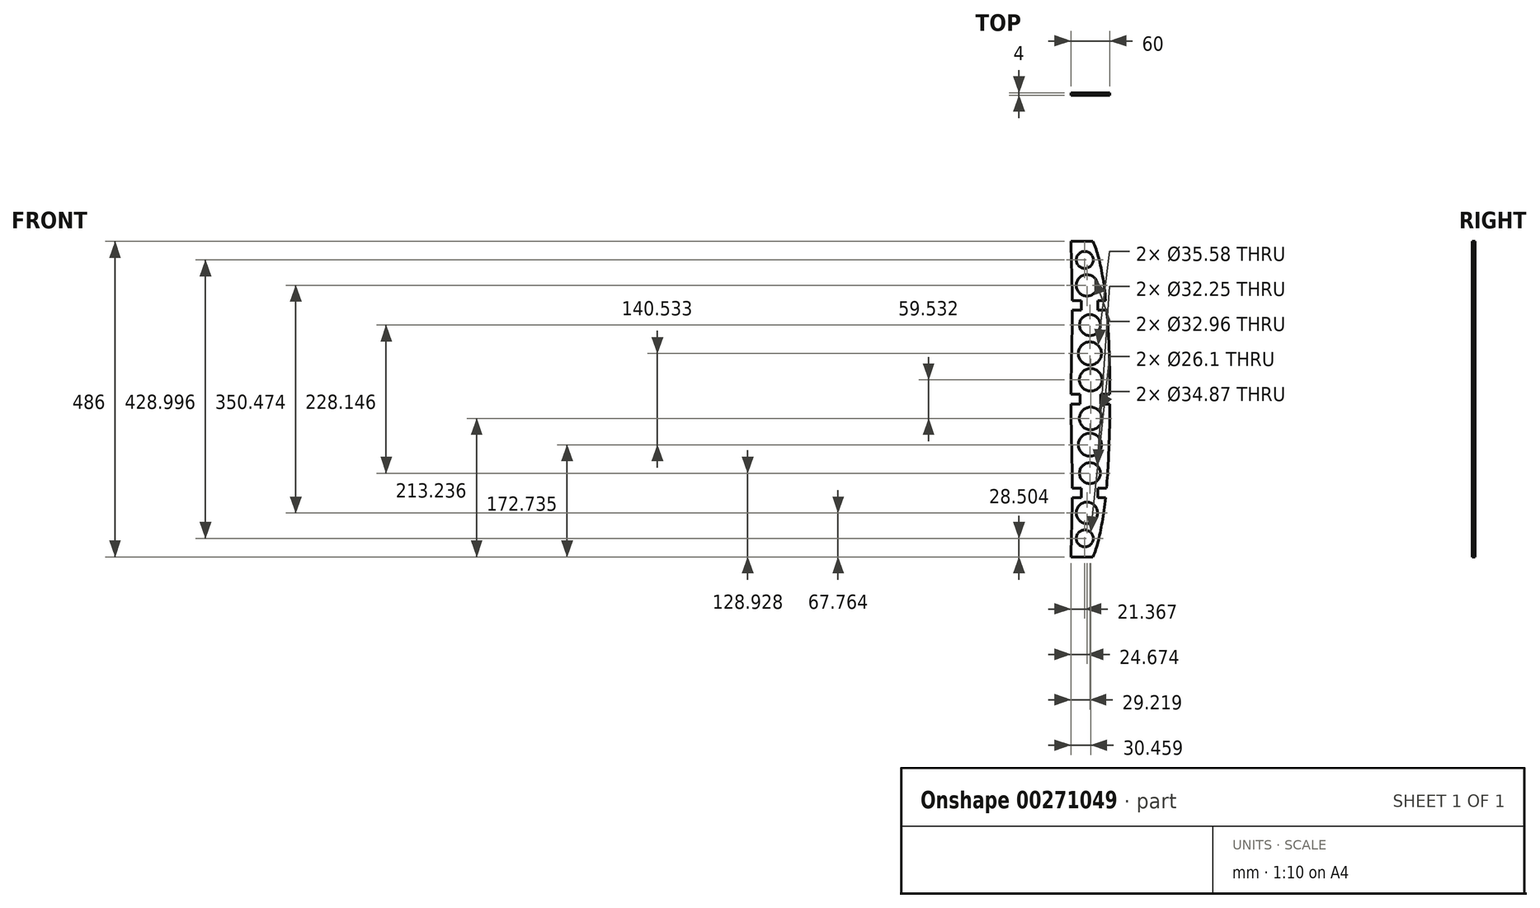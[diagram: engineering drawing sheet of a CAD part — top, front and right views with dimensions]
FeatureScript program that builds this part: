
annotation { "Feature Type Name" : "Feature", "Feature Type Description" : "" }
export const myFeature = defineFeature(function(context is Context, id is Id, definition is map)
    precondition{}
    {
        {
            var Q0;
            Q0=qCreatedBy(makeId("Front.planeOp"),FACE);
            var sketch = newSketch(context, id + "F0", { "sketchPlane" : qUnion([Q0])});
            skLineSegment(sketch, "E0", {"start": v(174.1, -34.57) * mm, "end": v(114.1, -34.57) * mm});
            skLineSegment(sketch, "E1", {"start": v(114.1, -34.57) * mm, "end": v(114.1, 208.43) * mm});
            skLineSegment(sketch, "E2", {"start": v(114.1, 208.43) * mm, "end": v(148.1, 208.43) * mm});
            skLineSegment(sketch, "E3.MirrorCS", {"start": v(114.1, -277.57) * mm, "end": v(148.1, -277.57) * mm});
            skLineSegment(sketch, "E4.MirrorCS", {"start": v(114.1, -34.57) * mm, "end": v(114.1, -277.57) * mm});
            skFitSpline(sketch, "E5", {"points": [v(148.1, 208.43) * mm, v(174.1, -34.57) * mm, v(148.1, -277.57) * mm], "startDerivative": vector(121.96, -265.32) * mm, "endDerivative": vector(-117.79, -277.83) * mm});
            skLineSegment(sketch, "E6", {"start": v(114.1, 86.93) * mm, "end": v(116.1, 86.93) * mm});
            skPoint(sketch, "E6.endSnap0", {"position": v(114.1, 86.93) * mm});
            skLineSegment(sketch, "E7", {"start": v(114.1, -156.07) * mm, "end": v(116.1, -156.07) * mm});
            skFitSpline(sketch, "E8", {"points": [v(114.1, 208.43) * mm, v(116.1, 86.93) * mm, v(114.1, -34.57) * mm, v(116.1, -156.07) * mm, v(114.1, -277.57) * mm], "startDerivative": vector(13.71, -486) * mm, "endDerivative": vector(-13.71, -486) * mm});
            skLineSegment(sketch, "E9", {"start": v(160.1, -34.57) * mm, "end": v(160.1, -27.07) * mm});
            skLineSegment(sketch, "E10", {"start": v(160.1, -27.07) * mm, "end": v(174.1, -27.07) * mm});
            skLineSegment(sketch, "E11", {"start": v(128.1, -34.57) * mm, "end": v(128.1, -27.07) * mm});
            skLineSegment(sketch, "E12", {"start": v(128.1, -27.07) * mm, "end": v(114.1, -27.07) * mm});
            skLineSegment(sketch, "E13.MirrorCS", {"start": v(160.1, -34.57) * mm, "end": v(160.1, -42.07) * mm});
            skLineSegment(sketch, "E14.MirrorCS", {"start": v(160.1, -42.07) * mm, "end": v(174.1, -42.07) * mm});
            skLineSegment(sketch, "E15.MirrorCS", {"start": v(128.1, -34.57) * mm, "end": v(128.1, -42.07) * mm});
            skLineSegment(sketch, "E16.MirrorCS", {"start": v(128.1, -42.07) * mm, "end": v(114.1, -42.07) * mm});
            skLineSegment(sketch, "E17", {"start": v(196.65, 109.93) * mm, "end": v(78.2, 109.93) * mm});
            skLineSegment(sketch, "E18", {"start": v(155.24, 109.93) * mm, "end": v(155.24, 102.43) * mm});
            skLineSegment(sketch, "E19", {"start": v(155.24, 102.43) * mm, "end": v(169.24, 102.43) * mm});
            skLineSegment(sketch, "E20", {"start": v(130.15, 109.93) * mm, "end": v(130.15, 102.43) * mm});
            skLineSegment(sketch, "E21", {"start": v(130.15, 102.43) * mm, "end": v(116.15, 102.43) * mm});
            skLineSegment(sketch, "E22.MirrorCS", {"start": v(130.15, 109.93) * mm, "end": v(130.15, 117.43) * mm});
            skLineSegment(sketch, "E23.MirrorCS", {"start": v(130.15, 117.43) * mm, "end": v(116.15, 117.43) * mm});
            skLineSegment(sketch, "E24.MirrorCS", {"start": v(155.24, 109.93) * mm, "end": v(155.24, 117.43) * mm});
            skLineSegment(sketch, "E25.MirrorCS", {"start": v(155.24, 117.43) * mm, "end": v(169.24, 117.43) * mm});
            skLineSegment(sketch, "E26", {"start": v(116.15, 117.43) * mm, "end": v(115.35, 117.43) * mm});
            skCircle(sketch, "E27", {"center": v(144.57, -4.8) * mm, "radius": 17.44 * mm});
            skCircle(sketch, "E28", {"center": v(143.33, 35.7) * mm, "radius": 17.79 * mm});
            skCircle(sketch, "E29", {"center": v(143.33, 79.5) * mm, "radius": 16.12 * mm});
            skCircle(sketch, "E30", {"center": v(138.78, 140.67) * mm, "radius": 16.48 * mm});
            skCircle(sketch, "E31", {"center": v(135.48, 179.93) * mm, "radius": 13.05 * mm});
            skCircle(sketch, "E32.MirrorC", {"center": v(144.57, -64.33) * mm, "radius": 17.44 * mm});
            skCircle(sketch, "E33.MirrorC", {"center": v(143.33, -104.83) * mm, "radius": 17.79 * mm});
            skCircle(sketch, "E34.MirrorC", {"center": v(143.33, -148.64) * mm, "radius": 16.12 * mm});
            skLineSegment(sketch, "E35.MirrorCS", {"start": v(116.15, -186.57) * mm, "end": v(115.35, -186.57) * mm});
            skLineSegment(sketch, "E36.MirrorCS", {"start": v(155.24, -179.07) * mm, "end": v(155.24, -171.57) * mm});
            skLineSegment(sketch, "E37.MirrorCS", {"start": v(130.15, -179.07) * mm, "end": v(130.15, -186.57) * mm});
            skLineSegment(sketch, "E38.MirrorCS", {"start": v(130.15, -179.07) * mm, "end": v(130.15, -171.57) * mm});
            skLineSegment(sketch, "E39.MirrorCS", {"start": v(155.24, -179.07) * mm, "end": v(155.24, -186.57) * mm});
            skLineSegment(sketch, "E40.MirrorCS", {"start": v(155.24, -171.57) * mm, "end": v(169.24, -171.57) * mm});
            skLineSegment(sketch, "E41.MirrorCS", {"start": v(155.24, -186.57) * mm, "end": v(169.24, -186.57) * mm});
            skLineSegment(sketch, "E42.MirrorCS", {"start": v(130.15, -186.57) * mm, "end": v(116.15, -186.57) * mm});
            skLineSegment(sketch, "E43.MirrorCS", {"start": v(130.15, -171.57) * mm, "end": v(116.15, -171.57) * mm});
            skCircle(sketch, "E44.MirrorC", {"center": v(138.78, -209.8) * mm, "radius": 16.48 * mm});
            skCircle(sketch, "E45.MirrorC", {"center": v(135.48, -249.07) * mm, "radius": 13.05 * mm});
            skLineSegment(sketch, "E46", {"start": v(116.15, -171.57) * mm, "end": v(115.43, -171.57) * mm});
            skSolve(sketch);
        }
        {
            var Q0;
            {var subQ8=sQuery(id+"F0.wireOp",EDGE,"E9");Q0=makeQuery(id+"F0.imprint","IMPRINT",FACE,{"disambiguationData":[TD([[makeQuery(id+"F0.imprint","IMPRINT",EDGE,{"derivedFrom":subQ8}),1.0]])]});}
            var Q1;
            {var subQ5=sQuery(id+"F0.wireOp",EDGE,"E2");Q1=makeQuery(id+"F0.imprint","IMPRINT",FACE,{"disambiguationData":[TD([[makeQuery(id+"F0.imprint","IMPRINT",EDGE,{"derivedFrom":subQ5}),-1.0]])]});}
            var Q2;
            {var subQ12=sQuery(id+"F0.wireOp",EDGE,"E3.MirrorCS");Q2=makeQuery(id+"F0.imprint","IMPRINT",FACE,{"disambiguationData":[TD([[makeQuery(id+"F0.imprint","IMPRINT",EDGE,{"derivedFrom":subQ12}),1.0]])]});}
            extrude(context, id + "F1", {"entities" : qUnion([Q0, Q1, Q2]), "depth" : 4 * mm});
        }
    });
